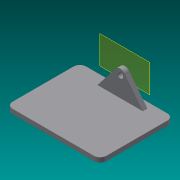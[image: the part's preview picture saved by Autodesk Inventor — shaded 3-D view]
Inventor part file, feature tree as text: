
AUTODESK INVENTOR PART (.ipt)
format: ipt  version: 2013 SP2 (Build 170200200, 200)  size: 101,888 bytes
history: native  units: in
note: dims shown in document units (in); Inventor stores cm internally (conversion verified against a paired STEP export)
features: reference x6, fillet x4, extrude x2, sketch x2, plane x1
ambient origin geometry x8: Origin, YZ Plane, XZ Plane, XY Plane, X Axis, Y Axis, Z Axis, Center Point
bodies: Solid1 (feature_tree)
feature tree (15):
  plane  "Work Plane1"
  extrude  "Extrusion1"  Depth=0.589in
  extrude  "Extrusion2"  Depth=0.0938in TaperAngle=0.0deg
  fillet  "Fillet1"  Radius=0.125in
  fillet  "Fillet2"  Radius=0.125in
  fillet  "Fillet3"  Radius=0.125in
  fillet  "Fillet4"  Radius=0.125in
  sketch  "Sketch1"  dims[d0=0.589in d1=0.589in]
  reference  "Reference1"
  sketch  "Sketch2"  dims[d2=0.0938in d3=0.0in d4=0.0938in d5=0.0in d6=0.125in d7=0.125in d8=0.125in d9=0.125in]
  reference  "Reference2"
  reference  "Reference3"
  reference  "Reference4"
  reference  "Reference5"
  reference  "Reference6"
